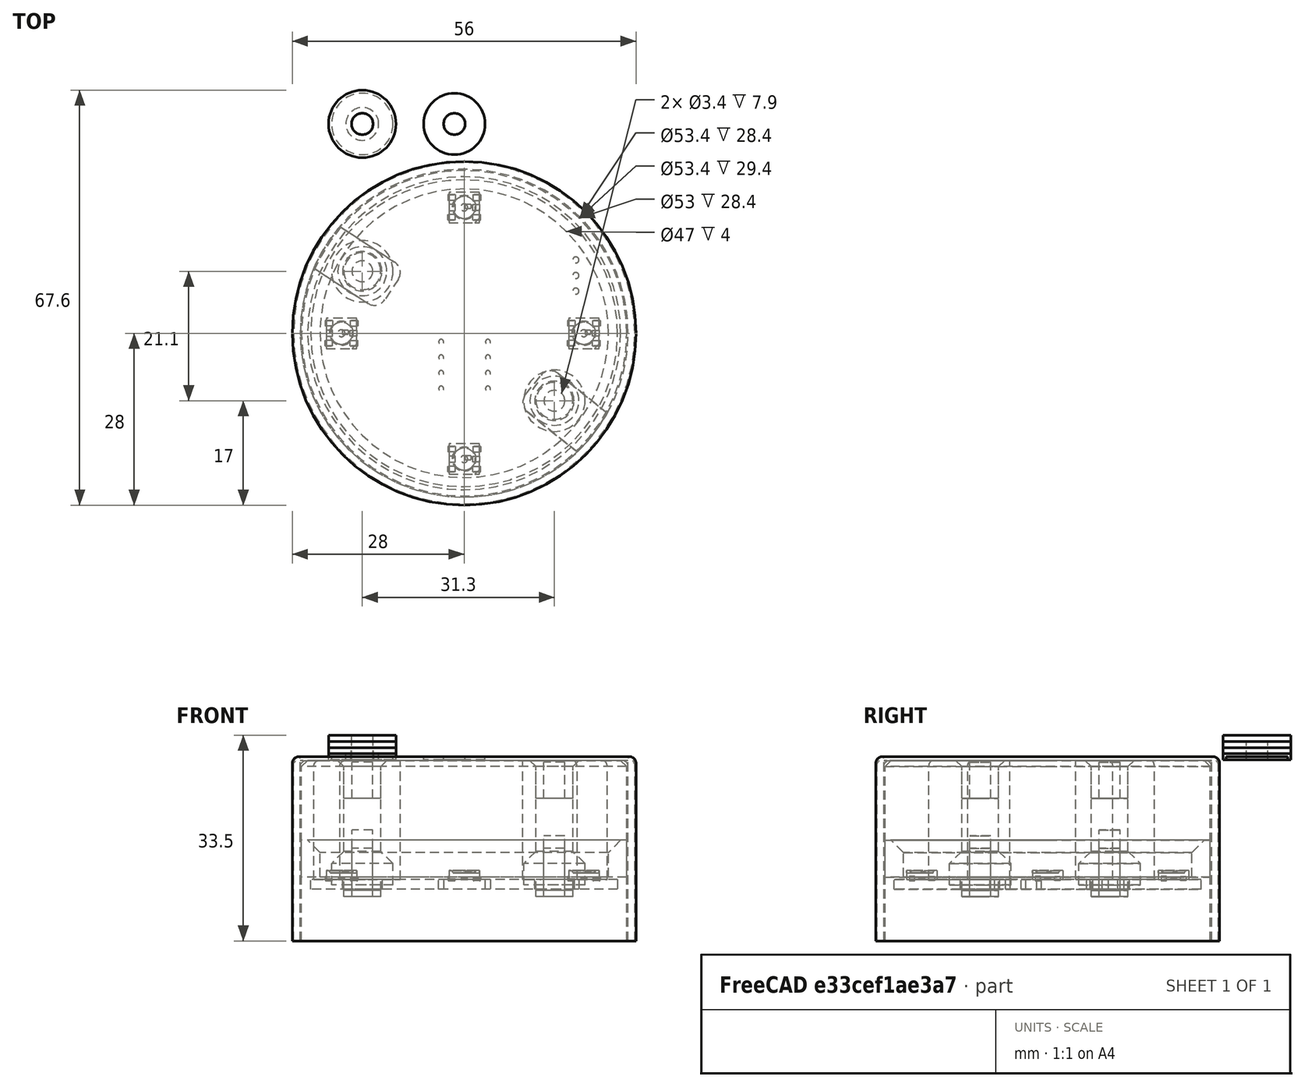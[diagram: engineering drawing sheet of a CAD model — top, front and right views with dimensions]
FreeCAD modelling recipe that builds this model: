
FCSTD DOCUMENT  (FreeCAD 0.19R)
Label: Base_PollFoll
License: All rights reserved
LicenseURL: http://en.wikipedia.org/wiki/All_rights_reserved
objects: Part::Cylinder×36, Part::Cut×16, Part::MultiFuse×6, Part::Feature×5, Part::Chamfer×5, Part::Fillet×5, App::Part×4, Part::Box×2, Sketcher::SketchObject×1
note: 76 computed .brp shape members not serialized (recipe doc carries the construction recipe); baked Part::Feature solids carry a one-line shape summary decoded from their .brp

FEATURE [Part::Feature] Pcb
  Placement = pos=(-148.5,98.5,0) rot=(0,0,1;0rad)
  shape: bbox 50 x 50 x 1.6 mm, 16 faces (baked)
FEATURE [Sketcher::SketchObject] PCB_Sketch
  sketch-geometry (3):
    g0: Circle CenterX=2.2 CenterY=8 CenterZ=0 NormalX=0 NormalY=0 NormalZ=1 AngleXU=0 Radius=3.2
    g1: Circle CenterX=-29.1 CenterY=29.1 CenterZ=0 NormalX=0 NormalY=0 NormalZ=1 AngleXU=0 Radius=3.2
    g2: Circle CenterX=-12.5 CenterY=19 CenterZ=0 NormalX=0 NormalY=0 NormalZ=1 AngleXU=0 Radius=25
FEATURE [App::Part] Board_Geoms
  Group = -> [Pcb,PCB_Sketch]
  Origin = -> Origin
FEATURE [Part::Feature] Shape  label="D4_risk1E78E08Bni4a_5D1F6ED0[2]"
  Placement = pos=(-32.5,19,0) rot=(0,0,-1;1.5708rad)
  shape: bbox 5.35 x 4.95 x 1.7 mm, 58 faces (baked)
FEATURE [Part::Feature] Shape001  label="D3_risk1E78E08Bni4a_5D1F6EBA[2]"
  Placement = pos=(-12.5,-1.5,0) rot=(0,0,-1;1.5708rad)
  shape: bbox 5.35 x 4.95 x 1.7 mm, 58 faces (baked)
FEATURE [Part::Feature] Shape002  label="D2_risk1E78E08Bni4a_5D1F6EA4[2]"
  Placement = pos=(7,19,0) rot=(0,0,-1;1.5708rad)
  shape: bbox 5.35 x 4.95 x 1.7 mm, 58 faces (baked)
FEATURE [Part::Feature] Shape003  label="D1_risk1E78E08Bni4a_5D1F6E8E[2]"
  Placement = pos=(-12.5,39.5,0) rot=(0,0,-1;1.5708rad)
  shape: bbox 5.35 x 4.95 x 1.7 mm, 58 faces (baked)
FEATURE [App::Part] Top
  Group = -> [Shape,Shape001,Shape002,Shape003]
  Origin = -> Origin003
FEATURE [App::Part] Step_Models
  Group = -> [Top]
  Origin = -> Origin002
FEATURE [App::Part] Board  label="PollFoll"
  Group = -> [Board_Geoms,Step_Models]
  Origin = -> Origin001
  Placement = pos=(0,0,0.2) rot=(0,0,1;0rad)
FEATURE [Part::Cylinder] Cylinder  label="base exterior vaciado"
  Angle = 360
  AttacherType = Attacher::AttachEngine3D
  Height = 30
  Placement = pos=(-12.5,19,-10.6) rot=(0,0,1;0rad)
  Radius = 26.5
FEATURE [Part::Cylinder] Cylinder001  label="base exterior"
  Angle = 360
  AttacherType = Attacher::AttachEngine3D
  Height = 30
  Placement = pos=(-12.5,19,-10) rot=(0,0,1;0rad)
  Radius = 27.8
FEATURE [Part::Cut] Cut
  Base = -> Cylinder001
  Refine = true
  Tool = -> Cylinder
FEATURE [Part::Cylinder] Cylinder002  label="Tope1"
  Angle = 360
  AttacherType = Attacher::AttachEngine3D
  Height = 6.5
  Placement = pos=(2.2,8,-2.8) rot=(0,0,1;0rad)
  Radius = 3
FEATURE [Part::Cylinder] Cylinder003  label="Tope2"
  Angle = 360
  AttacherType = Attacher::AttachEngine3D
  Height = 6.5
  Placement = pos=(-29.1,29.1,-2.8) rot=(0,0,1;0rad)
  Radius = 3
FEATURE [Part::Cylinder] Cylinder004  label="vaciado tope1"
  Angle = 360
  AttacherType = Attacher::AttachEngine3D
  Height = 6.5
  Placement = pos=(2.2,8,-3.4) rot=(0,0,1;0rad)
  Radius = 1.7
FEATURE [Part::Cylinder] Cylinder005  label="vaciado tope2"
  Angle = 360
  AttacherType = Attacher::AttachEngine3D
  Height = 6.5
  Placement = pos=(-29.1,29.1,-3.4) rot=(0,0,1;0rad)
  Radius = 1.7
FEATURE [Part::Cut] Cut001
  Base = -> Cylinder002
  Placement = pos=(0,0,16) rot=(0,0,1;0rad)
  Refine = true
  Tool = -> Cylinder004
FEATURE [Part::Cut] Cut002
  Base = -> Cylinder003
  Placement = pos=(0,0,16) rot=(0,0,1;0rad)
  Refine = true
  Tool = -> Cylinder005
FEATURE [Part::MultiFuse] Fusion
  Refine = true
  Shapes = -> [Cut002,Cut001,Cut]
FEATURE [Part::Chamfer] Chamfer
  Base = -> Fusion
  Edges = 3 edges r=1: [Edge1,Edge4,Edge5]
FEATURE [Part::Fillet] Fillet  label="base diseño alto"
  Base = -> Chamfer
  Edges = 1 edges r=1: [Edge21]
FEATURE [Part::Cylinder] Cylinder006  label="Tope003"
  Angle = 360
  AttacherType = Attacher::AttachEngine3D
  Height = 0.5
  Placement = pos=(-29.1,53.1,25.2) rot=(0,0,1;0rad)
  Radius = 5
FEATURE [Part::Cylinder] Cylinder007  label="vaciado tope003"
  Angle = 360
  AttacherType = Attacher::AttachEngine3D
  Height = 1.5
  Placement = pos=(-29.1,53.1,24.6) rot=(0,0,1;0rad)
  Radius = 1.75
FEATURE [Part::Cut] Cut003  label="arandela"
  Base = -> Cylinder006
  Placement = pos=(0,0,-5.7) rot=(0,0,1;0rad)
  Refine = true
  Tool = -> Cylinder007
FEATURE [Part::Cylinder] Cylinder008  label="vaciado tope004"
  Angle = 360
  AttacherType = Attacher::AttachEngine3D
  Height = 1.5
  Placement = pos=(-29.1,53.1,24.6) rot=(0,0,1;0rad)
  Radius = 1.75
FEATURE [Part::Cylinder] Cylinder009  label="Tope004"
  Angle = 360
  AttacherType = Attacher::AttachEngine3D
  Height = 0.5
  Placement = pos=(-29.1,53.1,25.2) rot=(0,0,1;0rad)
  Radius = 5
FEATURE [Part::Cut] Cut004  label="arandela001"
  Base = -> Cylinder009
  Placement = pos=(15,0,-5.7) rot=(0,0,1;0rad)
  Refine = true
  Tool = -> Cylinder008
FEATURE [Part::Cylinder] Cylinder010  label="Tope005"
  Angle = 360
  AttacherType = Attacher::AttachEngine3D
  Height = 1
  Placement = pos=(-29.1,53.1,25.2) rot=(0,0,1;0rad)
  Radius = 5.5
FEATURE [Part::Cylinder] Cylinder011  label="vaciado tope005"
  Angle = 360
  AttacherType = Attacher::AttachEngine3D
  Height = 5
  Placement = pos=(-29.1,53.1,24.6) rot=(0,0,1;0rad)
  Radius = 1.8
FEATURE [Part::Cut] Cut005  label="arandela_1mm"
  Base = -> Cylinder010
  Placement = pos=(0,0,-5.7) rot=(0,0,1;0rad)
  Refine = true
  Tool = -> Cylinder011
FEATURE [Part::Cylinder] Cylinder012  label="Tope006"
  Angle = 360
  AttacherType = Attacher::AttachEngine3D
  Height = 2
  Placement = pos=(-29.1,53.1,25.2) rot=(0,0,1;0rad)
  Radius = 5.5
FEATURE [Part::Cylinder] Cylinder013  label="vaciado tope006"
  Angle = 360
  AttacherType = Attacher::AttachEngine3D
  Height = 5
  Placement = pos=(-29.1,53.1,24.6) rot=(0,0,1;0rad)
  Radius = 1.8
FEATURE [Part::Cut] Cut006  label="arandela_2mm"
  Base = -> Cylinder012
  Placement = pos=(0,0,-5.7) rot=(0,0,1;0rad)
  Refine = true
  Tool = -> Cylinder013
FEATURE [Part::Cylinder] Cylinder014  label="vaciado tope007"
  Angle = 360
  AttacherType = Attacher::AttachEngine3D
  Height = 5
  Placement = pos=(-29.1,53.1,24.6) rot=(0,0,1;0rad)
  Radius = 1.8
FEATURE [Part::Cylinder] Cylinder015  label="Tope007"
  Angle = 360
  AttacherType = Attacher::AttachEngine3D
  Height = 3
  Placement = pos=(-29.1,53.1,25.2) rot=(0,0,1;0rad)
  Radius = 5.5
FEATURE [Part::Cut] Cut007  label="arandela_3mm"
  Base = -> Cylinder015
  Placement = pos=(0,0,-5.7) rot=(0,0,1;0rad)
  Refine = true
  Tool = -> Cylinder014
FEATURE [Part::Cylinder] Cylinder016  label="vaciado tope008"
  Angle = 360
  AttacherType = Attacher::AttachEngine3D
  Height = 5
  Placement = pos=(-29.1,53.1,24.6) rot=(0,0,1;0rad)
  Radius = 1.8
FEATURE [Part::Cylinder] Cylinder017  label="Tope008"
  Angle = 360
  AttacherType = Attacher::AttachEngine3D
  Height = 4
  Placement = pos=(-29.1,53.1,25.2) rot=(0,0,1;0rad)
  Radius = 5.5
FEATURE [Part::Cut] Cut008  label="arandela_4mm"
  Base = -> Cylinder017
  Placement = pos=(0,0,-5.7) rot=(0,0,1;0rad)
  Refine = true
  Tool = -> Cylinder016
FEATURE [Part::Cylinder] Cylinder018  label="base exterior vaciado001"
  Angle = 360
  AttacherType = Attacher::AttachEngine3D
  Height = 30
  Placement = pos=(-12.5,19,-10.6) rot=(0,0,1;0rad)
  Radius = 26.7
FEATURE [Part::Cylinder] Cylinder019  label="base exterior001"
  Angle = 360
  AttacherType = Attacher::AttachEngine3D
  Height = 30
  Placement = pos=(-12.5,19,-10) rot=(0,0,1;0rad)
  Radius = 28
FEATURE [Part::Cut] Cut011
  Base = -> Cylinder019
  Refine = true
  Tool = -> Cylinder018
FEATURE [Part::Cylinder] Cylinder020  label="Tope009"
  Angle = 360
  AttacherType = Attacher::AttachEngine3D
  Height = 5.5
  Placement = pos=(2.2,8,-1.8) rot=(0,0,1;0rad)
  Radius = 3
FEATURE [Part::Cylinder] Cylinder021  label="Tope010"
  Angle = 360
  AttacherType = Attacher::AttachEngine3D
  Height = 5.5
  Placement = pos=(-29.1,29.1,-1.8) rot=(0,0,1;0rad)
  Radius = 3
FEATURE [Part::Cylinder] Cylinder024  label="arco interior exterior"
  Angle = 360
  AttacherType = Attacher::AttachEngine3D
  Height = 6
  Placement = pos=(-12.5,19,-10.6) rot=(0,0,1;0rad)
  Radius = 26.5
FEATURE [Part::Cylinder] Cylinder025  label="arco interior vaciado"
  Angle = 360
  AttacherType = Attacher::AttachEngine3D
  Height = 6
  Placement = pos=(-12.5,19,-10.6) rot=(0,0,1;0rad)
  Radius = 23.5
FEATURE [Part::Cut] Cut012
  Base = -> Cylinder024
  Placement = pos=(0,0,11) rot=(0,0,1;0rad)
  Refine = true
  Tool = -> Cylinder025
FEATURE [Part::Box] Box  label="Cubo"
  AttacherType = Attacher::AttachEngine3D
  Height = 20
  Length = 8
  Placement = pos=(6.73913,-1.03233,0) rot=(0,0,1;0.890118rad)
  Width = 13.5
FEATURE [Part::Fillet] Fillet001  label="base"
  Base = -> Cut011
  Edges = 2 edges r=1: [Edge1,Edge6]
FEATURE [Part::Cylinder] Cylinder026  label="vaciado tope011"
  Angle = 360
  AttacherType = Attacher::AttachEngine3D
  Height = 11.5
  Placement = pos=(-29.1,29.1,-3.4) rot=(0,0,1;0rad)
  Radius = 1.7
FEATURE [Part::Cylinder] Cylinder027  label="vaciado tope012"
  Angle = 360
  AttacherType = Attacher::AttachEngine3D
  Height = 10.5
  Placement = pos=(2.2,8,-3.4) rot=(0,0,1;0rad)
  Radius = 1.7
FEATURE [Part::Cylinder] Cylinder029  label="base exterior vaciado002"
  Angle = 360
  AttacherType = Attacher::AttachEngine3D
  Height = 30
  Placement = pos=(-12.5,19,-10.6) rot=(0,0,1;0rad)
  Radius = 26.7
FEATURE [Part::Cylinder] Cylinder030  label="base exterior002"
  Angle = 360
  AttacherType = Attacher::AttachEngine3D
  Height = 30
  Placement = pos=(-12.5,19,-10) rot=(0,0,1;0rad)
  Radius = 28
FEATURE [Part::Cut] Cut016
  Base = -> Cylinder030
  Refine = true
  Tool = -> Cylinder029
FEATURE [Part::Fillet] Fillet002  label="base001"
  Base = -> Cut016
  Edges = 1 edges r=2: [Edge1]
FEATURE [Part::Cylinder] Cylinder031  label="Tope011"
  Angle = 360
  AttacherType = Attacher::AttachEngine3D
  Height = 22.5
  Placement = pos=(2.2,8,-2.8) rot=(0,0,1;0rad)
  Radius = 3
FEATURE [Part::Cylinder] Cylinder032  label="Tope012"
  Angle = 360
  AttacherType = Attacher::AttachEngine3D
  Height = 22.5
  Placement = pos=(-29.1,29.1,-2.8) rot=(0,0,1;0rad)
  Radius = 3
FEATURE [Part::Cylinder] Cylinder033  label="vaciado tope014"
  Angle = 360
  AttacherType = Attacher::AttachEngine3D
  Height = 8.5
  Placement = pos=(2.2,8,-3.4) rot=(0,0,1;0rad)
  Radius = 1.7
FEATURE [Part::Cylinder] Cylinder034  label="vaciado tope015"
  Angle = 360
  AttacherType = Attacher::AttachEngine3D
  Height = 8.5
  Placement = pos=(-29.1,29.1,-3.4) rot=(0,0,1;0rad)
  Radius = 1.7
FEATURE [Part::Cylinder] Cylinder035  label="Tope013"
  Angle = 360
  AttacherType = Attacher::AttachEngine3D
  Height = 5.5
  Placement = pos=(-29.1,29.1,-0.9) rot=(0,0,1;0rad)
  Radius = 5
FEATURE [Part::Cylinder] Cylinder036  label="Tope014"
  Angle = 360
  AttacherType = Attacher::AttachEngine3D
  Height = 5.5
  Placement = pos=(2.2,8,-0.9) rot=(0,0,1;0rad)
  Radius = 5
FEATURE [Part::Chamfer] Chamfer008
  Base = -> Cylinder036
  Edges = 1 edges r=2: [Edge1]
FEATURE [Part::MultiFuse] Fusion003
  Refine = true
  Shapes = -> [Cylinder031,Chamfer008]
FEATURE [Part::Cut] Cut017  label="columna1"
  Base = -> Fusion003
  Refine = true
  Tool = -> Cylinder033
FEATURE [Part::Chamfer] Chamfer009
  Base = -> Cylinder035
  Edges = 1 edges r=2: [Edge1]
FEATURE [Part::MultiFuse] Fusion004
  Refine = true
  Shapes = -> [Cylinder032,Chamfer009]
FEATURE [Part::Cut] Cut018  label="columna2"
  Base = -> Fusion004
  Refine = true
  Tool = -> Cylinder034
FEATURE [Part::MultiFuse] Fusion005
  Refine = true
  Shapes = -> [Fillet002,Cut017,Cut018]
FEATURE [Part::Chamfer] Chamfer010  label="base version OK pilares001"
  Base = -> Fusion005
  Edges = 2 edges r=1: [Edge9,Edge10]
FEATURE [Part::Chamfer] Chamfer013  label="aro"
  Base = -> Cut012
  Edges = 1 edges r=2: [Edge4]
FEATURE [Part::Fillet] Fillet003  label="fijacion1"
  Base = -> Box
  Edges = 3 edges: [Edge3 r=2,Edge7 r=2,Edge10 r=2.5]
FEATURE [Part::Box] Box001  label="Cubo001"
  AttacherType = Attacher::AttachEngine3D
  Height = 20
  Length = 8
  Placement = pos=(-33.4718,36.8552,2e-15) rot=(0,0,1;4.13643rad)
  Width = 13.5
FEATURE [Part::Fillet] Fillet004  label="fijacion002"
  Base = -> Box001
  Edges = 3 edges: [Edge3 r=2,Edge7 r=2,Edge10 r=2.5]
FEATURE [Part::MultiFuse] Fusion006
  Refine = true
  Shapes = -> [Fillet003,Fillet001,Fillet004,Cylinder021,Cylinder020]
FEATURE [Part::MultiFuse] Fusion007  label="vaciados de M3"
  Refine = true
  Shapes = -> [Cylinder026,Cylinder027]
FEATURE [Part::Cut] Cut019  label="base v10 FINAL"
  Base = -> Fusion006
  Refine = true
  Tool = -> Fusion007
FEATURE [Part::Cylinder] Cylinder037  label="Tope015"
  Angle = 360
  AttacherType = Attacher::AttachEngine3D
  Height = 1
  Placement = pos=(-29.1,53.1,25.2) rot=(0,0,1;0rad)
  Radius = 2.675
  expr: Radius = 5.35 / 2
FEATURE [Part::Cylinder] Cylinder038  label="vaciado tope016"
  Angle = 360
  AttacherType = Attacher::AttachEngine3D
  Height = 3.5
  Placement = pos=(-29.1,53.1,24.6) rot=(0,0,1;0rad)
  Radius = 1.85
FEATURE [Part::Cut] Cut020  label="arandela_2mm001"
  Base = -> Cylinder037
  Placement = pos=(0,0,-5.7) rot=(0,0,1;0rad)
  Refine = true
  Tool = -> Cylinder038
